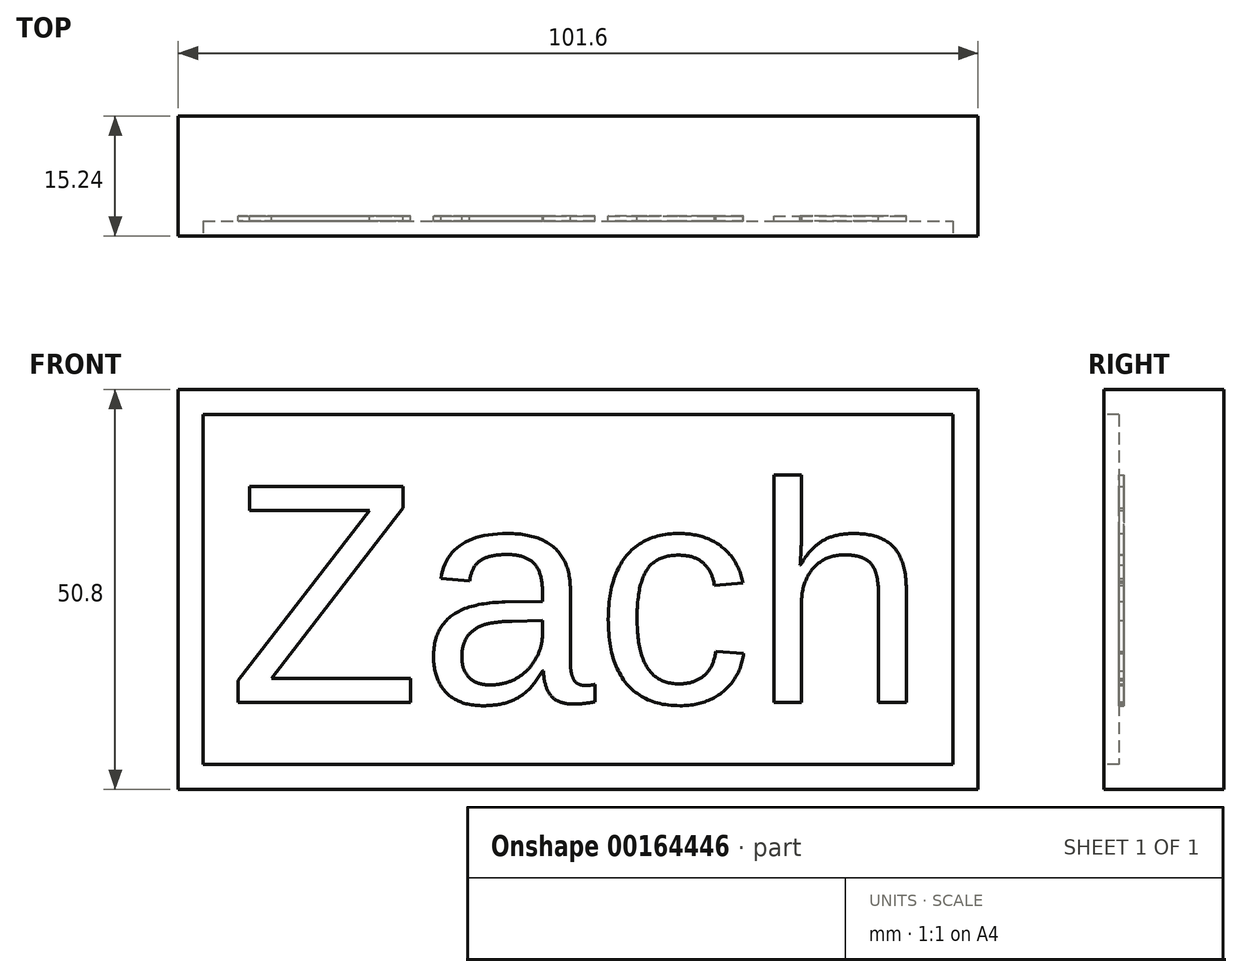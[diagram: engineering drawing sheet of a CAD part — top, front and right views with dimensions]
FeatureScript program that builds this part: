
annotation { "Feature Type Name" : "Feature", "Feature Type Description" : "" }
export const myFeature = defineFeature(function(context is Context, id is Id, definition is map)
    precondition{}
    {
        {
            var Q0;
            Q0=qCreatedBy(makeId("Front.planeOp"),FACE);
            var sketch = newSketch(context, id + "F0", { "sketchPlane" : qUnion([Q0])});
            skLineSegment(sketch, "E0.bottom", {"start": v(-50.8, 25.4) * mm, "end": v(50.8, 25.4) * mm});
            skLineSegment(sketch, "E0.top", {"start": v(-50.8, -25.4) * mm, "end": v(50.8, -25.4) * mm});
            skLineSegment(sketch, "E0.left", {"start": v(-50.8, 25.4) * mm, "end": v(-50.8, -25.4) * mm});
            skLineSegment(sketch, "E0.right", {"start": v(50.8, 25.4) * mm, "end": v(50.8, -25.4) * mm});
            skSolve(sketch);
        }
        {
            var Q0;
            Q0=makeQuery(id+"F0.imprint","IMPRINT",FACE,{"disambiguationData":[TD([[makeQuery(id+"F0.imprint","IMPRINT",EDGE,{"derivedFrom":sQuery(id+"F0.wireOp",EDGE,"E0.bottom")}),-1.0]])]});
            extrude(context, id + "F1", {"entities" : qUnion([Q0]), "depth" : 2.54 * mm, "hasSecondDirection" : true, "secondDirectionOppositeDirection" : true, "secondDirectionDepth" : 12.7 * mm});
        }
        {
            var Q0;
            Q0=qCreatedBy(makeId("Front.planeOp"),FACE);
            var sketch = newSketch(context, id + "F2", { "sketchPlane" : qUnion([Q0])});
            skText(sketch, "E1", { "text": "Zach", "fontName": "Arimo-Regular.ttf"});
            const initialGuessF2  = {"E1": [-0.04445, -0.01437, 1, 0, 0.02874]};
            skSetInitialGuess(sketch, initialGuessF2);
            skSolve(sketch);
        }
        {
            var Q0;
            Q0 = qSketchRegion(id + "F2", true);
            extrude(context, id + "F3", {"entities" : qUnion([Q0]), "operationType" : NewBodyOperationType.REMOVE, "depth" : 25.4 * mm});
        }
        {
            var Q0;
            {var subQ0=sQuery(id+"F0.wireOp",EDGE,"E0.top");var subQ1=sQuery(id+"F0.wireOp",EDGE,"E0.right");var subQ2=sQuery(id+"F0.wireOp",EDGE,"E0.bottom");var subQ3=sQuery(id+"F0.wireOp",EDGE,"E0.left");Q0=makeQuery(id+"F3.boolean.opBoolean","SPLIT",FACE,{"disambiguationData":[TD([makeQuery(id+"F1.opExtrude","SWEPT_FACE",FACE,{"disambiguationData":[OSD([subQ2])]})])],"derivedFrom":makeQuery(id+"F1.opExtrude","CAP_FACE",FACE,{"disambiguationData":[OSD([subQ2,subQ0,subQ3,subQ1])],"isStart":false})});}
            var sketch = newSketch(context, id + "F4", { "sketchPlane" : qUnion([Q0])});
            skLineSegment(sketch, "E2.bottom", {"start": v(-47.63, 22.22) * mm, "end": v(47.63, 22.23) * mm});
            skLineSegment(sketch, "E2.top", {"start": v(-47.63, -22.23) * mm, "end": v(47.63, -22.22) * mm});
            skLineSegment(sketch, "E2.left", {"start": v(-47.63, 22.22) * mm, "end": v(-47.63, -22.23) * mm});
            skLineSegment(sketch, "E2.right", {"start": v(47.63, 22.23) * mm, "end": v(47.63, -22.22) * mm});
            skSolve(sketch);
        }
        {
            var Q0;
            Q0=makeQuery(id+"F4.imprint","IMPRINT",FACE,{"disambiguationData":[TD([[makeQuery(id+"F4.imprint","IMPRINT",EDGE,{"derivedFrom":sQuery(id+"F4.wireOp",EDGE,"E2.bottom")}),-1.0]])]});
            var Q1;
            {var subQ0=makeQuery(id+"F1.opExtrude","CAP_FACE",FACE,{"disambiguationData":[OSD([sQuery(id+"F0.wireOp",EDGE,"E0.bottom"),sQuery(id+"F0.wireOp",EDGE,"E0.top"),sQuery(id+"F0.wireOp",EDGE,"E0.left"),sQuery(id+"F0.wireOp",EDGE,"E0.right")])],"isStart":false});Q1=makeQuery(id+"F4.imprint","IMPRINT",FACE,{"disambiguationData":[TD([[makeQuery(id+"F4.imprint","IMPRINT",EDGE,{"derivedFrom":makeQuery(id+"F3.boolean.opBoolean","INTERSECT",EDGE,{"derivedFrom":[subQ0,makeQuery(id+"F3.opExtrude","SWEPT_FACE",FACE,{"disambiguationData":[OSD([sQuery(id+"F2.wireOp",EDGE,"E1.sketch_text.stroke-10")])]})]})}),1.0]])]});}
            extrude(context, id + "F5", {"entities" : qUnion([Q0, Q1]), "operationType" : NewBodyOperationType.REMOVE, "oppositeDirection" : true, "depth" : 1.9 * mm});
        }
    });
